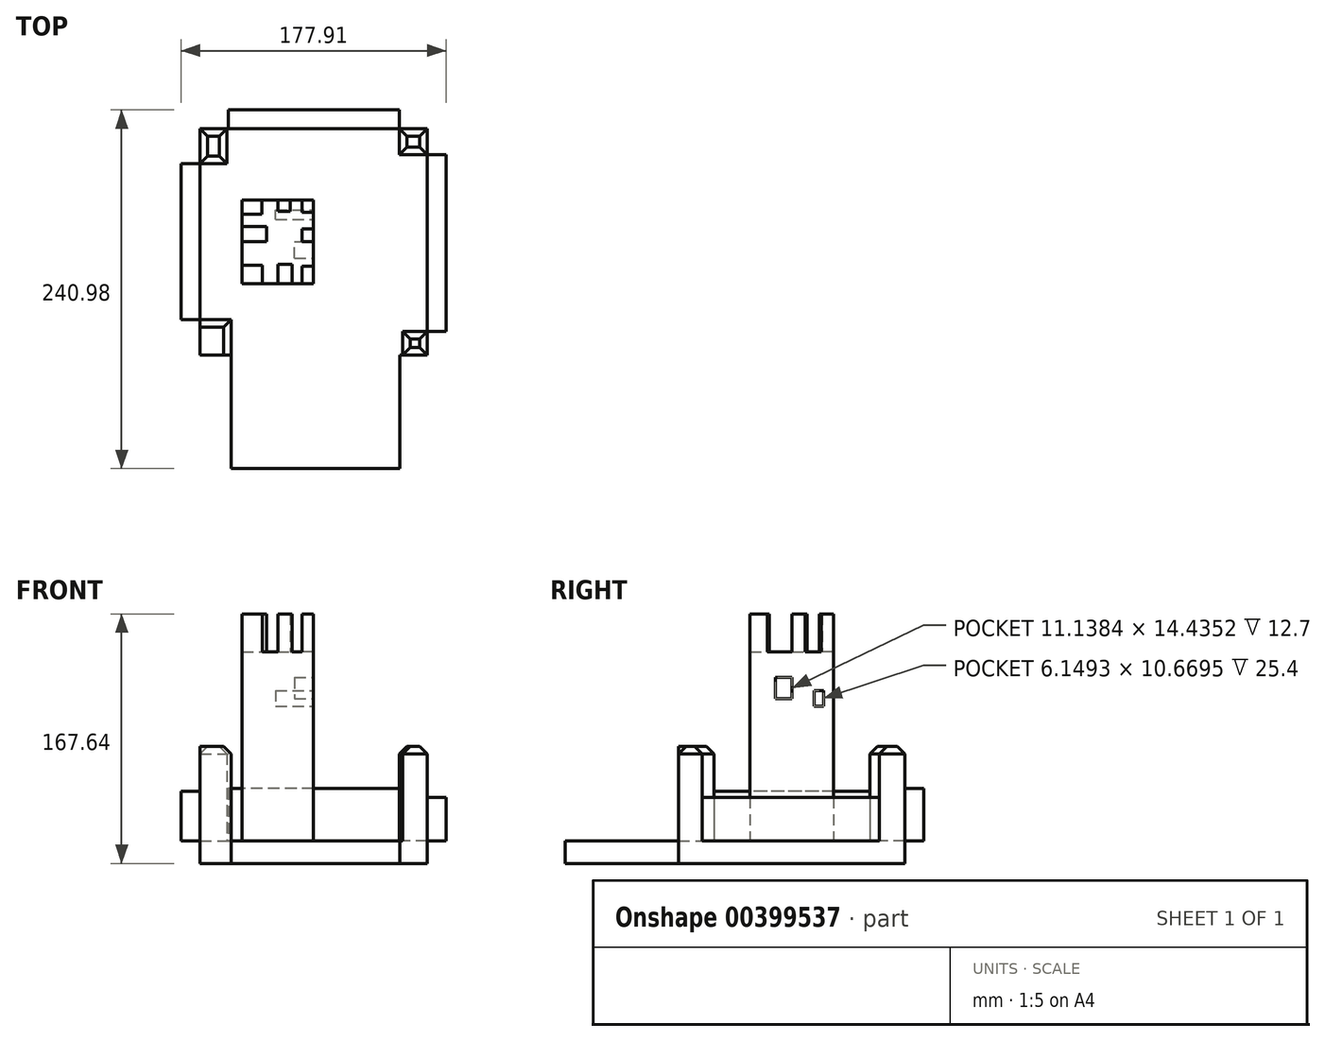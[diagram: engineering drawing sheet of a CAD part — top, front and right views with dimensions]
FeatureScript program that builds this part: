
annotation { "Feature Type Name" : "Feature", "Feature Type Description" : "" }
export const myFeature = defineFeature(function(context is Context, id is Id, definition is map)
    precondition{}
    {
        {
            var Q0;
            Q0=qCreatedBy(makeId("Top.planeOp"),FACE);
            var sketch = newSketch(context, id + "F0", { "sketchPlane" : qUnion([Q0])});
            skLineSegment(sketch, "E0.bottom", {"start": v(-76.09, -76.33) * mm, "end": v(76.42, -76.33) * mm});
            skLineSegment(sketch, "E0.top", {"start": v(-76.09, 75.75) * mm, "end": v(76.42, 75.75) * mm});
            skLineSegment(sketch, "E0.left", {"start": v(-76.09, -76.33) * mm, "end": v(-76.09, 75.75) * mm});
            skLineSegment(sketch, "E0.right", {"start": v(76.42, -76.33) * mm, "end": v(76.42, 75.75) * mm});
            skSolve(sketch);
        }
        {
            var Q0;
            Q0=makeQuery(id+"F0.imprint","IMPRINT",FACE,{"disambiguationData":[TD([[makeQuery(id+"F0.imprint","IMPRINT",EDGE,{"derivedFrom":sQuery(id+"F0.wireOp",EDGE,"E0.bottom")}),1.0]])]});
            extrude(context, id + "F1", {"entities" : qUnion([Q0]), "depth" : 2.54 * mm});
        }
        {
            var Q0;
            Q0=makeQuery(id+"F1.opExtrude","CAP_FACE",FACE,{"disambiguationData":[OSD([sQuery(id+"F0.wireOp",EDGE,"E0.bottom"),sQuery(id+"F0.wireOp",EDGE,"E0.top"),sQuery(id+"F0.wireOp",EDGE,"E0.left"),sQuery(id+"F0.wireOp",EDGE,"E0.right")])],"isStart":false});
            var sketch = newSketch(context, id + "F2", { "sketchPlane" : qUnion([Q0])});
            skLineSegment(sketch, "E1.bottom", {"start": v(-76.09, -76.33) * mm, "end": v(-55.24, -76.33) * mm});
            skLineSegment(sketch, "E1.top", {"start": v(-76.09, -52.31) * mm, "end": v(-55.24, -52.31) * mm});
            skLineSegment(sketch, "E1.left", {"start": v(-76.09, -76.33) * mm, "end": v(-76.09, -52.31) * mm});
            skLineSegment(sketch, "E1.right", {"start": v(-55.24, -76.33) * mm, "end": v(-55.24, -52.31) * mm});
            skLineSegment(sketch, "E2.bottom", {"start": v(-76.09, 75.75) * mm, "end": v(-58.26, 75.75) * mm});
            skLineSegment(sketch, "E2.top", {"start": v(-76.09, 52.46) * mm, "end": v(-58.26, 52.46) * mm});
            skLineSegment(sketch, "E2.left", {"start": v(-76.09, 75.75) * mm, "end": v(-76.09, 52.46) * mm});
            skLineSegment(sketch, "E2.right", {"start": v(-58.26, 75.75) * mm, "end": v(-58.26, 52.46) * mm});
            skLineSegment(sketch, "E3.bottom", {"start": v(76.42, -76.33) * mm, "end": v(60.04, -76.33) * mm});
            skLineSegment(sketch, "E3.top", {"start": v(76.42, -60.24) * mm, "end": v(60.04, -60.24) * mm});
            skLineSegment(sketch, "E3.left", {"start": v(76.42, -76.33) * mm, "end": v(76.42, -60.24) * mm});
            skLineSegment(sketch, "E3.right", {"start": v(60.04, -76.33) * mm, "end": v(60.04, -60.24) * mm});
            skLineSegment(sketch, "E4.bottom", {"start": v(76.42, 75.75) * mm, "end": v(57.79, 75.75) * mm});
            skLineSegment(sketch, "E4.top", {"start": v(76.42, 58.6) * mm, "end": v(57.79, 58.6) * mm});
            skLineSegment(sketch, "E4.left", {"start": v(76.42, 75.75) * mm, "end": v(76.42, 58.6) * mm});
            skLineSegment(sketch, "E4.right", {"start": v(57.79, 75.75) * mm, "end": v(57.79, 58.6) * mm});
            skSolve(sketch);
        }
        {
            var Q0;
            Q0=makeQuery(id+"F2.imprint","IMPRINT",FACE,{"disambiguationData":[TD([[makeQuery(id+"F2.imprint","IMPRINT",EDGE,{"derivedFrom":sQuery(id+"F2.wireOp",EDGE,"E1.bottom")}),1.0]])]});
            extrude(context, id + "F3", {"entities" : qUnion([Q0]), "operationType" : NewBodyOperationType.ADD, "depth" : 76.2 * mm});
        }
        {
            var Q0;
            Q0=makeQuery(id+"F2.imprint","IMPRINT",FACE,{"disambiguationData":[TD([[makeQuery(id+"F2.imprint","IMPRINT",EDGE,{"derivedFrom":sQuery(id+"F2.wireOp",EDGE,"E2.bottom")}),-1.0]])]});
            extrude(context, id + "F4", {"entities" : qUnion([Q0]), "operationType" : NewBodyOperationType.ADD, "depth" : 76.2 * mm});
        }
        {
            var Q0;
            Q0=makeQuery(id+"F2.imprint","IMPRINT",FACE,{"disambiguationData":[TD([[makeQuery(id+"F2.imprint","IMPRINT",EDGE,{"derivedFrom":sQuery(id+"F2.wireOp",EDGE,"E3.bottom")}),1.0]])]});
            var Q1;
            Q1=makeQuery(id+"F2.imprint","IMPRINT",FACE,{"disambiguationData":[TD([[makeQuery(id+"F2.imprint","IMPRINT",EDGE,{"derivedFrom":sQuery(id+"F2.wireOp",EDGE,"E4.bottom")}),-1.0]])]});
            extrude(context, id + "F5", {"entities" : qUnion([Q0, Q1]), "operationType" : NewBodyOperationType.ADD, "depth" : 76.2 * mm});
        }
        {
            var Q0;
            Q0=makeQuery(id+"F3.opExtrude","CAP_FACE",FACE,{"disambiguationData":[OSD([sQuery(id+"F2.wireOp",EDGE,"E1.bottom"),sQuery(id+"F2.wireOp",EDGE,"E1.top"),sQuery(id+"F2.wireOp",EDGE,"E1.left"),sQuery(id+"F2.wireOp",EDGE,"E1.right")])],"isStart":false});
            extrude(context, id + "F6", {"entities" : qUnion([Q0]), "operationType" : NewBodyOperationType.REMOVE, "oppositeDirection" : true, "depth" : 12.7 * mm});
        }
        {
            var Q0;
            {var subQ6=sQuery(id+"F2.wireOp",EDGE,"E1.top");Q0=makeQuery(id+"F2.imprint","IMPRINT",FACE,{"disambiguationData":[TD([[makeQuery(id+"F2.imprint","IMPRINT",EDGE,{"derivedFrom":subQ6}),1.0]])]});}
            var Q1;
            Q1=makeQuery(id+"F6.boolean.opBoolean","COPY",FACE,{"derivedFrom":makeQuery(id+"F6.opExtrude","CAP_FACE",FACE,{"disambiguationData":[OSD([sQuery(id+"F2.wireOp",EDGE,"E1.bottom"),sQuery(id+"F2.wireOp",EDGE,"E1.top"),sQuery(id+"F2.wireOp",EDGE,"E1.left"),sQuery(id+"F2.wireOp",EDGE,"E1.right")])],"isStart":false})});
            extrude(context, id + "F7", {"entities" : qUnion([Q0, Q1]), "operationType" : NewBodyOperationType.ADD, "depth" : 12.7 * mm});
        }
        {
            var Q0;
            Q0=makeQuery(id+"F7.opExtrude","CAP_EDGE",EDGE,{"disambiguationData":[OSD([sQuery(id+"F2.wireOp",EDGE,"E1.bottom")])],"isStart":false});
            var Q1;
            {var subQ0=sQuery(id+"F2.wireOp",EDGE,"E1.right");Q1=makeQuery(id+"F7.opExtrude","CAP_EDGE",EDGE,{"disambiguationData":[OSD([subQ0]),TDD([makeQuery(id+"F6.boolean.opBoolean","COPY",EDGE,{"derivedFrom":makeQuery(id+"F6.opExtrude","CAP_EDGE",EDGE,{"disambiguationData":[OSD([subQ0])],"isStart":false})})])],"isStart":false});}
            var Q2;
            {var subQ0=sQuery(id+"F2.wireOp",EDGE,"E1.top");Q2=makeQuery(id+"F7.opExtrude","CAP_EDGE",EDGE,{"disambiguationData":[OSD([subQ0]),TDD([makeQuery(id+"F6.boolean.opBoolean","COPY",EDGE,{"derivedFrom":makeQuery(id+"F6.opExtrude","CAP_EDGE",EDGE,{"disambiguationData":[OSD([subQ0])],"isStart":false})})])],"isStart":false});}
            var Q3;
            Q3=makeQuery(id+"F7.opExtrude","CAP_EDGE",EDGE,{"disambiguationData":[OSD([sQuery(id+"F2.wireOp",EDGE,"E1.left")])],"isStart":false});
            chamfer(context, id + "F8", {"entities" : qUnion([Q0, Q1, Q2, Q3]), "width" : 5.08 * mm, "tangentPropagation" : true});
        }
        {
            var Q0;
            Q0=makeQuery(id+"F4.opExtrude","CAP_EDGE",EDGE,{"disambiguationData":[OSD([sQuery(id+"F2.wireOp",EDGE,"E2.top")])],"isStart":false});
            var Q1;
            Q1=makeQuery(id+"F4.opExtrude","CAP_EDGE",EDGE,{"disambiguationData":[OSD([sQuery(id+"F2.wireOp",EDGE,"E2.right")])],"isStart":false});
            var Q2;
            Q2=makeQuery(id+"F4.opExtrude","CAP_EDGE",EDGE,{"disambiguationData":[OSD([sQuery(id+"F2.wireOp",EDGE,"E2.left")])],"isStart":false});
            var Q3;
            Q3=makeQuery(id+"F4.opExtrude","CAP_EDGE",EDGE,{"disambiguationData":[OSD([sQuery(id+"F2.wireOp",EDGE,"E2.bottom")])],"isStart":false});
            chamfer(context, id + "F9", {"entities" : qUnion([Q0, Q1, Q2, Q3]), "width" : 5.08 * mm, "tangentPropagation" : true});
        }
        {
            var Q0;
            Q0=makeQuery(id+"F5.opExtrude","CAP_EDGE",EDGE,{"disambiguationData":[OSD([sQuery(id+"F2.wireOp",EDGE,"E3.bottom")])],"isStart":false});
            var Q1;
            Q1=makeQuery(id+"F5.opExtrude","CAP_EDGE",EDGE,{"disambiguationData":[OSD([sQuery(id+"F2.wireOp",EDGE,"E3.left")])],"isStart":false});
            var Q2;
            Q2=makeQuery(id+"F5.opExtrude","CAP_EDGE",EDGE,{"disambiguationData":[OSD([sQuery(id+"F2.wireOp",EDGE,"E3.right")])],"isStart":false});
            var Q3;
            Q3=makeQuery(id+"F5.opExtrude","CAP_EDGE",EDGE,{"disambiguationData":[OSD([sQuery(id+"F2.wireOp",EDGE,"E3.top")])],"isStart":false});
            chamfer(context, id + "F10", {"entities" : qUnion([Q0, Q1, Q2, Q3]), "width" : 5.08 * mm, "tangentPropagation" : true});
        }
        {
            var Q0;
            Q0=makeQuery(id+"F5.opExtrude","CAP_EDGE",EDGE,{"disambiguationData":[OSD([sQuery(id+"F2.wireOp",EDGE,"E4.top")])],"isStart":false});
            var Q1;
            Q1=makeQuery(id+"F5.opExtrude","CAP_EDGE",EDGE,{"disambiguationData":[OSD([sQuery(id+"F2.wireOp",EDGE,"E4.left")])],"isStart":false});
            var Q2;
            Q2=makeQuery(id+"F5.opExtrude","CAP_EDGE",EDGE,{"disambiguationData":[OSD([sQuery(id+"F2.wireOp",EDGE,"E4.right")])],"isStart":false});
            var Q3;
            Q3=makeQuery(id+"F5.opExtrude","CAP_EDGE",EDGE,{"disambiguationData":[OSD([sQuery(id+"F2.wireOp",EDGE,"E4.bottom")])],"isStart":false});
            chamfer(context, id + "F11", {"entities" : qUnion([Q0, Q1, Q2, Q3]), "width" : 5.08 * mm, "tangentPropagation" : true});
        }
        {
            var Q0;
            {var subQ0=sQuery(id+"F0.wireOp",EDGE,"E0.right");Q0=makeQuery(id+"F7.boolean.opBoolean","MERGE",FACE,{"derivedFrom":[makeQuery(id+"F5.boolean.opBoolean","MERGE",FACE,{"derivedFrom":[makeQuery(id+"F1.opExtrude","SWEPT_FACE",FACE,{"disambiguationData":[OSD([subQ0])]}),makeQuery(id+"F5.opExtrude","SWEPT_FACE",FACE,{"disambiguationData":[OSD([sQuery(id+"F2.wireOp",EDGE,"E3.left")])]}),makeQuery(id+"F5.opExtrude","SWEPT_FACE",FACE,{"disambiguationData":[OSD([sQuery(id+"F2.wireOp",EDGE,"E4.left")])]})]}),makeQuery(id+"F7.opExtrude","SWEPT_FACE",FACE,{"disambiguationData":[OSD([subQ0])]})]});}
            var sketch = newSketch(context, id + "F12", { "sketchPlane" : qUnion([Q0])});
            skLineSegment(sketch, "E5.bottom", {"start": v(-60.24, 44.45) * mm, "end": v(58.6, 44.45) * mm});
            skLineSegment(sketch, "E5.top", {"start": v(-60.24, 15.24) * mm, "end": v(58.6, 15.24) * mm});
            skLineSegment(sketch, "E5.left", {"start": v(-60.24, 44.45) * mm, "end": v(-60.24, 15.24) * mm});
            skLineSegment(sketch, "E5.right", {"start": v(58.6, 44.45) * mm, "end": v(58.6, 15.24) * mm});
            skSolve(sketch);
        }
        {
            var Q0;
            Q0=makeQuery(id+"F12.imprint","IMPRINT",FACE,{"disambiguationData":[TD([[makeQuery(id+"F12.imprint","IMPRINT",EDGE,{"derivedFrom":sQuery(id+"F12.wireOp",EDGE,"E5.bottom")}),-1.0]])]});
            extrude(context, id + "F13", {"entities" : qUnion([Q0]), "depth" : 12.7 * mm});
        }
        {
            var Q0;
            {var subQ0=sQuery(id+"F0.wireOp",EDGE,"E0.top");Q0=makeQuery(id+"F7.boolean.opBoolean","MERGE",FACE,{"derivedFrom":[makeQuery(id+"F5.boolean.opBoolean","MERGE",FACE,{"derivedFrom":[makeQuery(id+"F4.boolean.opBoolean","MERGE",FACE,{"derivedFrom":[makeQuery(id+"F1.opExtrude","SWEPT_FACE",FACE,{"disambiguationData":[OSD([subQ0])]}),makeQuery(id+"F4.opExtrude","SWEPT_FACE",FACE,{"disambiguationData":[OSD([sQuery(id+"F2.wireOp",EDGE,"E2.bottom")])]})]}),makeQuery(id+"F5.opExtrude","SWEPT_FACE",FACE,{"disambiguationData":[OSD([sQuery(id+"F2.wireOp",EDGE,"E4.bottom")])]})]}),makeQuery(id+"F7.opExtrude","SWEPT_FACE",FACE,{"disambiguationData":[OSD([subQ0])]})]});}
            var sketch = newSketch(context, id + "F14", { "sketchPlane" : qUnion([Q0])});
            skSolve(sketch);
        }
        {
            var Q0;
            {var subQ1=sQuery(id+"F0.wireOp",EDGE,"E0.top");Q0=makeQuery(id+"F14.imprint","IMPRINT",FACE,{"disambiguationData":[TD([[makeQuery(id+"F14.imprint","IMPRINT",EDGE,{"derivedFrom":makeQuery(id+"F1.opExtrude","CAP_EDGE",EDGE,{"disambiguationData":[OSD([subQ1])],"isStart":true})}),-1.0]])]});}
            var sketch = newSketch(context, id + "F15", { "sketchPlane" : qUnion([Q0])});
            skLineSegment(sketch, "E6.bottom", {"start": v(-58.9, 50.23) * mm, "end": v(57.3, 50.23) * mm});
            skLineSegment(sketch, "E6.top", {"start": v(-58.9, 14.67) * mm, "end": v(57.3, 14.67) * mm});
            skLineSegment(sketch, "E6.left", {"start": v(-58.9, 50.23) * mm, "end": v(-58.9, 14.67) * mm});
            skLineSegment(sketch, "E6.right", {"start": v(57.3, 50.23) * mm, "end": v(57.3, 14.67) * mm});
            skSolve(sketch);
        }
        {
            var Q0;
            {var subQ0=sQuery(id+"F15.wireOp",EDGE,"E6.right");var subQ1=sQuery(id+"F15.wireOp",EDGE,"E6.bottom");var subQ2=makeQuery(id+"F15.imprint","INTERSECT",VERTEX,{"derivedFrom":[subQ1,subQ0]});Q0=makeQuery(id+"F15.imprint","IMPRINT",FACE,{"disambiguationData":[TD([[makeQuery(id+"F15.imprint","IMPRINT",EDGE,{"disambiguationData":[TD([[subQ2,-1.0]])],"derivedFrom":subQ0}),-1.0]])]});}
            extrude(context, id + "F16", {"entities" : qUnion([Q0]), "depth" : 12.7 * mm});
        }
        {
            var Q0;
            {var subQ0=sQuery(id+"F2.wireOp",EDGE,"E1.left");var subQ1=sQuery(id+"F0.wireOp",EDGE,"E0.left");Q0=makeQuery(id+"F7.boolean.opBoolean","MERGE",FACE,{"derivedFrom":[makeQuery(id+"F4.boolean.opBoolean","MERGE",FACE,{"derivedFrom":[makeQuery(id+"F3.boolean.opBoolean","MERGE",FACE,{"derivedFrom":[makeQuery(id+"F1.opExtrude","SWEPT_FACE",FACE,{"disambiguationData":[OSD([subQ1])]}),makeQuery(id+"F3.opExtrude","SWEPT_FACE",FACE,{"disambiguationData":[OSD([subQ0])]})]}),makeQuery(id+"F4.opExtrude","SWEPT_FACE",FACE,{"disambiguationData":[OSD([sQuery(id+"F2.wireOp",EDGE,"E2.left")])]})]}),makeQuery(id+"F7.opExtrude","SWEPT_FACE",FACE,{"disambiguationData":[OSD([subQ1])]}),makeQuery(id+"F7.opExtrude","SWEPT_FACE",FACE,{"disambiguationData":[OSD([subQ0])]})]});}
            var sketch = newSketch(context, id + "F17", { "sketchPlane" : qUnion([Q0])});
            skLineSegment(sketch, "E7.bottom", {"start": v(-52.46, 48.54) * mm, "end": v(52.31, 48.54) * mm});
            skLineSegment(sketch, "E7.top", {"start": v(-52.46, 15.24) * mm, "end": v(52.31, 15.24) * mm});
            skLineSegment(sketch, "E7.left", {"start": v(-52.46, 48.54) * mm, "end": v(-52.46, 15.24) * mm});
            skLineSegment(sketch, "E7.right", {"start": v(52.31, 48.54) * mm, "end": v(52.31, 15.24) * mm});
            skSolve(sketch);
        }
        {
            var Q0;
            Q0 = qSketchRegion(id + "F17", true);
            extrude(context, id + "F18", {"entities" : qUnion([Q0]), "depth" : 12.7 * mm});
        }
        {
            var Q0;
            {var subQ0=sQuery(id+"F2.wireOp",EDGE,"E1.bottom");var subQ1=sQuery(id+"F0.wireOp",EDGE,"E0.bottom");Q0=makeQuery(id+"F7.boolean.opBoolean","MERGE",FACE,{"derivedFrom":[makeQuery(id+"F5.boolean.opBoolean","MERGE",FACE,{"derivedFrom":[makeQuery(id+"F3.boolean.opBoolean","MERGE",FACE,{"derivedFrom":[makeQuery(id+"F1.opExtrude","SWEPT_FACE",FACE,{"disambiguationData":[OSD([subQ1])]}),makeQuery(id+"F3.opExtrude","SWEPT_FACE",FACE,{"disambiguationData":[OSD([subQ0])]})]}),makeQuery(id+"F5.opExtrude","SWEPT_FACE",FACE,{"disambiguationData":[OSD([sQuery(id+"F2.wireOp",EDGE,"E3.bottom")])]})]}),makeQuery(id+"F7.opExtrude","SWEPT_FACE",FACE,{"disambiguationData":[OSD([subQ1])]}),makeQuery(id+"F7.opExtrude","SWEPT_FACE",FACE,{"disambiguationData":[OSD([subQ0])]})]});}
            var sketch = newSketch(context, id + "F19", { "sketchPlane" : qUnion([Q0])});
            skLineSegment(sketch, "E8.bottom", {"start": v(-55.24, 15.24) * mm, "end": v(58.19, 15.24) * mm});
            skLineSegment(sketch, "E8.top", {"start": v(-55.24, 0) * mm, "end": v(58.19, 0) * mm});
            skLineSegment(sketch, "E8.left", {"start": v(-55.24, 15.24) * mm, "end": v(-55.24, 0) * mm});
            skLineSegment(sketch, "E8.right", {"start": v(58.19, 15.24) * mm, "end": v(58.19, 0) * mm});
            skSolve(sketch);
        }
        {
            var Q0;
            Q0=makeQuery(id+"F19.imprint","IMPRINT",FACE,{"disambiguationData":[TD([[makeQuery(id+"F19.imprint","IMPRINT",EDGE,{"derivedFrom":sQuery(id+"F19.wireOp",EDGE,"E8.bottom")}),-1.0]])]});
            extrude(context, id + "F20", {"entities" : qUnion([Q0]), "operationType" : NewBodyOperationType.ADD, "depth" : 76.2 * mm});
        }
        {
            var Q0;
            {var subQ0=sQuery(id+"F2.wireOp",EDGE,"E1.bottom");var subQ3=sQuery(id+"F0.wireOp",EDGE,"E0.left");var subQ5=sQuery(id+"F0.wireOp",EDGE,"E0.bottom");Q0=makeQuery(id+"F20.boolean.opBoolean","SPLIT",FACE,{"disambiguationData":[TD([makeQuery(id+"F1.opExtrude","SWEPT_FACE",FACE,{"disambiguationData":[OSD([subQ3])]})])],"derivedFrom":makeQuery(id+"F7.boolean.opBoolean","MERGE",FACE,{"derivedFrom":[makeQuery(id+"F5.boolean.opBoolean","MERGE",FACE,{"derivedFrom":[makeQuery(id+"F3.boolean.opBoolean","MERGE",FACE,{"derivedFrom":[makeQuery(id+"F1.opExtrude","SWEPT_FACE",FACE,{"disambiguationData":[OSD([subQ5])]}),makeQuery(id+"F3.opExtrude","SWEPT_FACE",FACE,{"disambiguationData":[OSD([subQ0])]})]}),makeQuery(id+"F5.opExtrude","SWEPT_FACE",FACE,{"disambiguationData":[OSD([sQuery(id+"F2.wireOp",EDGE,"E3.bottom")])]})]}),makeQuery(id+"F7.opExtrude","SWEPT_FACE",FACE,{"disambiguationData":[OSD([subQ5])]}),makeQuery(id+"F7.opExtrude","SWEPT_FACE",FACE,{"disambiguationData":[OSD([subQ0])]})]})});}
            var sketch = newSketch(context, id + "F21", { "sketchPlane" : qUnion([Q0])});
            skLineSegment(sketch, "E9", {"start": v(-55.24, 55.44) * mm, "end": v(-125.52, -44.2) * mm});
            skLineSegment(sketch, "E10", {"start": v(-125.52, -44.2) * mm, "end": v(-19.06, -47.17) * mm});
            skLineSegment(sketch, "E11", {"start": v(-19.06, -47.17) * mm, "end": v(60.87, 66.14) * mm});
            skSolve(sketch);
        }
        {
            var Q0;
            Q0=makeQuery(id+"F20.boolean.opBoolean","MERGE",FACE,{"derivedFrom":[makeQuery(id+"F7.opExtrude","CAP_FACE",FACE,{"disambiguationData":[OSD([sQuery(id+"F0.wireOp",EDGE,"E0.bottom"),sQuery(id+"F0.wireOp",EDGE,"E0.top"),sQuery(id+"F0.wireOp",EDGE,"E0.left"),sQuery(id+"F0.wireOp",EDGE,"E0.right"),sQuery(id+"F2.wireOp",EDGE,"E1.top"),sQuery(id+"F2.wireOp",EDGE,"E1.right"),sQuery(id+"F2.wireOp",EDGE,"E2.top"),sQuery(id+"F2.wireOp",EDGE,"E2.right"),sQuery(id+"F2.wireOp",EDGE,"E3.top"),sQuery(id+"F2.wireOp",EDGE,"E3.right"),sQuery(id+"F2.wireOp",EDGE,"E4.top"),sQuery(id+"F2.wireOp",EDGE,"E4.right")])],"isStart":false}),makeQuery(id+"F20.opExtrude","SWEPT_FACE",FACE,{"disambiguationData":[OSD([sQuery(id+"F19.wireOp",EDGE,"E8.bottom")])]})]});
            var sketch = newSketch(context, id + "F22", { "sketchPlane" : qUnion([Q0])});
            skLineSegment(sketch, "E12.bottom", {"start": v(-47.93, 27.86) * mm, "end": v(0, 27.86) * mm});
            skLineSegment(sketch, "E12.top", {"start": v(-47.93, -28.25) * mm, "end": v(0, -28.25) * mm});
            skLineSegment(sketch, "E12.left", {"start": v(-47.93, 27.86) * mm, "end": v(-47.93, -28.25) * mm});
            skLineSegment(sketch, "E12.right", {"start": v(0, 27.86) * mm, "end": v(0, -28.25) * mm});
            skSolve(sketch);
        }
        {
            var Q0;
            Q0=makeQuery(id+"F22.imprint","IMPRINT",FACE,{"disambiguationData":[TD([[makeQuery(id+"F22.imprint","IMPRINT",EDGE,{"derivedFrom":sQuery(id+"F22.wireOp",EDGE,"E12.bottom")}),-1.0]])]});
            extrude(context, id + "F23", {"entities" : qUnion([Q0]), "operationType" : NewBodyOperationType.ADD, "depth" : 127 * mm});
        }
        {
            var Q0;
            Q0=makeQuery(id+"F23.opExtrude","CAP_FACE",FACE,{"disambiguationData":[OSD([sQuery(id+"F22.wireOp",EDGE,"E12.bottom"),sQuery(id+"F22.wireOp",EDGE,"E12.top"),sQuery(id+"F22.wireOp",EDGE,"E12.left"),sQuery(id+"F22.wireOp",EDGE,"E12.right")])],"isStart":false});
            var sketch = newSketch(context, id + "F24", { "sketchPlane" : qUnion([Q0])});
            skLineSegment(sketch, "E13.bottom", {"start": v(-47.93, -28.25) * mm, "end": v(-34.42, -28.25) * mm});
            skLineSegment(sketch, "E13.top", {"start": v(-47.93, -15.76) * mm, "end": v(-34.42, -15.76) * mm});
            skLineSegment(sketch, "E13.left", {"start": v(-47.93, -28.25) * mm, "end": v(-47.93, -15.76) * mm});
            skLineSegment(sketch, "E13.right", {"start": v(-34.42, -28.25) * mm, "end": v(-34.42, -15.76) * mm});
            skLineSegment(sketch, "E14.bottom", {"start": v(-47.93, 0) * mm, "end": v(-31.54, 0) * mm});
            skLineSegment(sketch, "E14.top", {"start": v(-47.93, 10.15) * mm, "end": v(-31.54, 10.15) * mm});
            skLineSegment(sketch, "E14.left", {"start": v(-47.93, 0) * mm, "end": v(-47.93, 10.15) * mm});
            skLineSegment(sketch, "E14.right", {"start": v(-31.54, 0) * mm, "end": v(-31.54, 10.15) * mm});
            skLineSegment(sketch, "E15.bottom", {"start": v(-47.93, 27.86) * mm, "end": v(-34.7, 27.86) * mm});
            skLineSegment(sketch, "E15.top", {"start": v(-47.93, 18.5) * mm, "end": v(-34.7, 18.5) * mm});
            skLineSegment(sketch, "E15.left", {"start": v(-47.93, 27.86) * mm, "end": v(-47.93, 18.5) * mm});
            skLineSegment(sketch, "E15.right", {"start": v(-34.7, 27.86) * mm, "end": v(-34.7, 18.5) * mm});
            skLineSegment(sketch, "E16.bottom", {"start": v(-23.97, -28.25) * mm, "end": v(-14.27, -28.25) * mm});
            skLineSegment(sketch, "E16.top", {"start": v(-23.97, -15.19) * mm, "end": v(-14.27, -15.19) * mm});
            skLineSegment(sketch, "E16.left", {"start": v(-23.97, -28.25) * mm, "end": v(-23.97, -15.19) * mm});
            skLineSegment(sketch, "E16.right", {"start": v(-14.27, -28.25) * mm, "end": v(-14.27, -15.19) * mm});
            skLineSegment(sketch, "E17.bottom", {"start": v(0, -28.25) * mm, "end": v(-7.64, -28.25) * mm});
            skLineSegment(sketch, "E17.top", {"start": v(0, -16.63) * mm, "end": v(-7.64, -16.63) * mm});
            skLineSegment(sketch, "E17.left", {"start": v(0, -28.25) * mm, "end": v(0, -16.63) * mm});
            skLineSegment(sketch, "E17.right", {"start": v(-7.64, -28.25) * mm, "end": v(-7.64, -16.63) * mm});
            skLineSegment(sketch, "E18.bottom", {"start": v(0, 0) * mm, "end": v(-7.64, 0) * mm});
            skLineSegment(sketch, "E18.top", {"start": v(0, 8.71) * mm, "end": v(-7.64, 8.71) * mm});
            skLineSegment(sketch, "E18.left", {"start": v(0, 0) * mm, "end": v(0, 8.71) * mm});
            skLineSegment(sketch, "E18.right", {"start": v(-7.64, 0) * mm, "end": v(-7.64, 8.71) * mm});
            skLineSegment(sketch, "E19.bottom", {"start": v(0, 27.86) * mm, "end": v(-7.64, 27.86) * mm});
            skLineSegment(sketch, "E19.top", {"start": v(0, 19.65) * mm, "end": v(-7.64, 19.65) * mm});
            skLineSegment(sketch, "E19.left", {"start": v(0, 27.86) * mm, "end": v(0, 19.65) * mm});
            skLineSegment(sketch, "E19.right", {"start": v(-7.64, 27.86) * mm, "end": v(-7.64, 19.65) * mm});
            skLineSegment(sketch, "E20.bottom", {"start": v(-23.97, 27.86) * mm, "end": v(-15.7, 27.86) * mm});
            skLineSegment(sketch, "E20.top", {"start": v(-23.97, 20.23) * mm, "end": v(-15.7, 20.23) * mm});
            skLineSegment(sketch, "E20.left", {"start": v(-23.97, 27.86) * mm, "end": v(-23.97, 20.23) * mm});
            skLineSegment(sketch, "E20.right", {"start": v(-15.7, 27.86) * mm, "end": v(-15.7, 20.23) * mm});
            skSolve(sketch);
        }
        {
            var Q0;
            Q0=makeQuery(id+"F24.imprint","IMPRINT",FACE,{"disambiguationData":[TD([[makeQuery(id+"F24.imprint","IMPRINT",EDGE,{"derivedFrom":sQuery(id+"F24.wireOp",EDGE,"E13.bottom")}),1.0]])]});
            extrude(context, id + "F25", {"entities" : qUnion([Q0]), "operationType" : NewBodyOperationType.ADD, "depth" : 25.4 * mm});
        }
        {
            var Q0;
            Q0=makeQuery(id+"F24.imprint","IMPRINT",FACE,{"disambiguationData":[TD([[makeQuery(id+"F24.imprint","IMPRINT",EDGE,{"derivedFrom":sQuery(id+"F24.wireOp",EDGE,"E14.bottom")}),1.0]])]});
            extrude(context, id + "F26", {"entities" : qUnion([Q0]), "operationType" : NewBodyOperationType.ADD, "depth" : 25.4 * mm});
        }
        {
            var Q0;
            Q0=makeQuery(id+"F24.imprint","IMPRINT",FACE,{"disambiguationData":[TD([[makeQuery(id+"F24.imprint","IMPRINT",EDGE,{"derivedFrom":sQuery(id+"F24.wireOp",EDGE,"E15.bottom")}),-1.0]])]});
            extrude(context, id + "F27", {"entities" : qUnion([Q0]), "operationType" : NewBodyOperationType.ADD, "depth" : 25.4 * mm});
        }
        {
            var Q0;
            Q0=makeQuery(id+"F24.imprint","IMPRINT",FACE,{"disambiguationData":[TD([[makeQuery(id+"F24.imprint","IMPRINT",EDGE,{"derivedFrom":sQuery(id+"F24.wireOp",EDGE,"E20.bottom")}),-1.0]])]});
            extrude(context, id + "F28", {"entities" : qUnion([Q0]), "operationType" : NewBodyOperationType.ADD, "depth" : 25.4 * mm});
        }
        {
            var Q0;
            Q0=makeQuery(id+"F24.imprint","IMPRINT",FACE,{"disambiguationData":[TD([[makeQuery(id+"F24.imprint","IMPRINT",EDGE,{"derivedFrom":sQuery(id+"F24.wireOp",EDGE,"E19.bottom")}),-1.0]])]});
            extrude(context, id + "F29", {"entities" : qUnion([Q0]), "operationType" : NewBodyOperationType.ADD, "depth" : 25.4 * mm});
        }
        {
            var Q0;
            Q0=makeQuery(id+"F24.imprint","IMPRINT",FACE,{"disambiguationData":[TD([[makeQuery(id+"F24.imprint","IMPRINT",EDGE,{"derivedFrom":sQuery(id+"F24.wireOp",EDGE,"E18.bottom")}),-1.0]])]});
            extrude(context, id + "F30", {"entities" : qUnion([Q0]), "operationType" : NewBodyOperationType.ADD, "depth" : 25.4 * mm});
        }
        {
            var Q0;
            Q0=makeQuery(id+"F24.imprint","IMPRINT",FACE,{"disambiguationData":[TD([[makeQuery(id+"F24.imprint","IMPRINT",EDGE,{"derivedFrom":sQuery(id+"F24.wireOp",EDGE,"E17.bottom")}),1.0]])]});
            extrude(context, id + "F31", {"entities" : qUnion([Q0]), "operationType" : NewBodyOperationType.ADD, "depth" : 25.4 * mm});
        }
        {
            var Q0;
            Q0=makeQuery(id+"F24.imprint","IMPRINT",FACE,{"disambiguationData":[TD([[makeQuery(id+"F24.imprint","IMPRINT",EDGE,{"derivedFrom":sQuery(id+"F24.wireOp",EDGE,"E16.bottom")}),1.0]])]});
            extrude(context, id + "F32", {"entities" : qUnion([Q0]), "operationType" : NewBodyOperationType.ADD, "depth" : 25.4 * mm});
        }
        {
            var Q0;
            Q0=makeQuery(id+"F31.boolean.opBoolean","MERGE",FACE,{"derivedFrom":[makeQuery(id+"F30.boolean.opBoolean","MERGE",FACE,{"derivedFrom":[makeQuery(id+"F29.boolean.opBoolean","MERGE",FACE,{"derivedFrom":[makeQuery(id+"F23.opExtrude","SWEPT_FACE",FACE,{"disambiguationData":[OSD([sQuery(id+"F22.wireOp",EDGE,"E12.right")])]}),makeQuery(id+"F29.opExtrude","SWEPT_FACE",FACE,{"disambiguationData":[OSD([sQuery(id+"F24.wireOp",EDGE,"E19.left")])]})]}),makeQuery(id+"F30.opExtrude","SWEPT_FACE",FACE,{"disambiguationData":[OSD([sQuery(id+"F24.wireOp",EDGE,"E18.left")])]})]}),makeQuery(id+"F31.opExtrude","SWEPT_FACE",FACE,{"disambiguationData":[OSD([sQuery(id+"F24.wireOp",EDGE,"E17.left")])]})]});
            var sketch = newSketch(context, id + "F33", { "sketchPlane" : qUnion([Q0])});
            skLineSegment(sketch, "E21.bottom", {"start": v(-11.14, 124.96) * mm, "end": v(0, 124.96) * mm});
            skLineSegment(sketch, "E21.top", {"start": v(-11.14, 110.53) * mm, "end": v(0, 110.53) * mm});
            skLineSegment(sketch, "E21.left", {"start": v(-11.14, 124.96) * mm, "end": v(-11.14, 110.53) * mm});
            skLineSegment(sketch, "E21.right", {"start": v(0, 124.96) * mm, "end": v(0, 110.53) * mm});
            skLineSegment(sketch, "E22.bottom", {"start": v(15, 116.17) * mm, "end": v(21.15, 116.17) * mm});
            skLineSegment(sketch, "E22.top", {"start": v(15, 105.5) * mm, "end": v(21.15, 105.5) * mm});
            skLineSegment(sketch, "E22.left", {"start": v(15, 116.17) * mm, "end": v(15, 105.5) * mm});
            skLineSegment(sketch, "E22.right", {"start": v(21.15, 116.17) * mm, "end": v(21.15, 105.5) * mm});
            skSolve(sketch);
        }
        {
            var Q0;
            Q0=makeQuery(id+"F33.imprint","IMPRINT",FACE,{"disambiguationData":[TD([[makeQuery(id+"F33.imprint","IMPRINT",EDGE,{"derivedFrom":sQuery(id+"F33.wireOp",EDGE,"E21.bottom")}),-1.0]])]});
            extrude(context, id + "F34", {"entities" : qUnion([Q0]), "operationType" : NewBodyOperationType.REMOVE, "oppositeDirection" : true, "depth" : 12.7 * mm});
        }
        {
            var Q0;
            Q0=makeQuery(id+"F33.imprint","IMPRINT",FACE,{"disambiguationData":[TD([[makeQuery(id+"F33.imprint","IMPRINT",EDGE,{"derivedFrom":sQuery(id+"F33.wireOp",EDGE,"E22.bottom")}),-1.0]])]});
            extrude(context, id + "F35", {"entities" : qUnion([Q0]), "operationType" : NewBodyOperationType.REMOVE, "oppositeDirection" : true, "depth" : 25.4 * mm});
        }
        {
            var Q0;
            Q0=sQuery(id+"F21.wireOp",EDGE,"E9");
            extrude(context, id + "F36", {"bodyType" : ToolBodyType.SURFACE, "surfaceEntities" : qUnion([Q0]), "depth" : 2.54 * mm});
        }
    });
